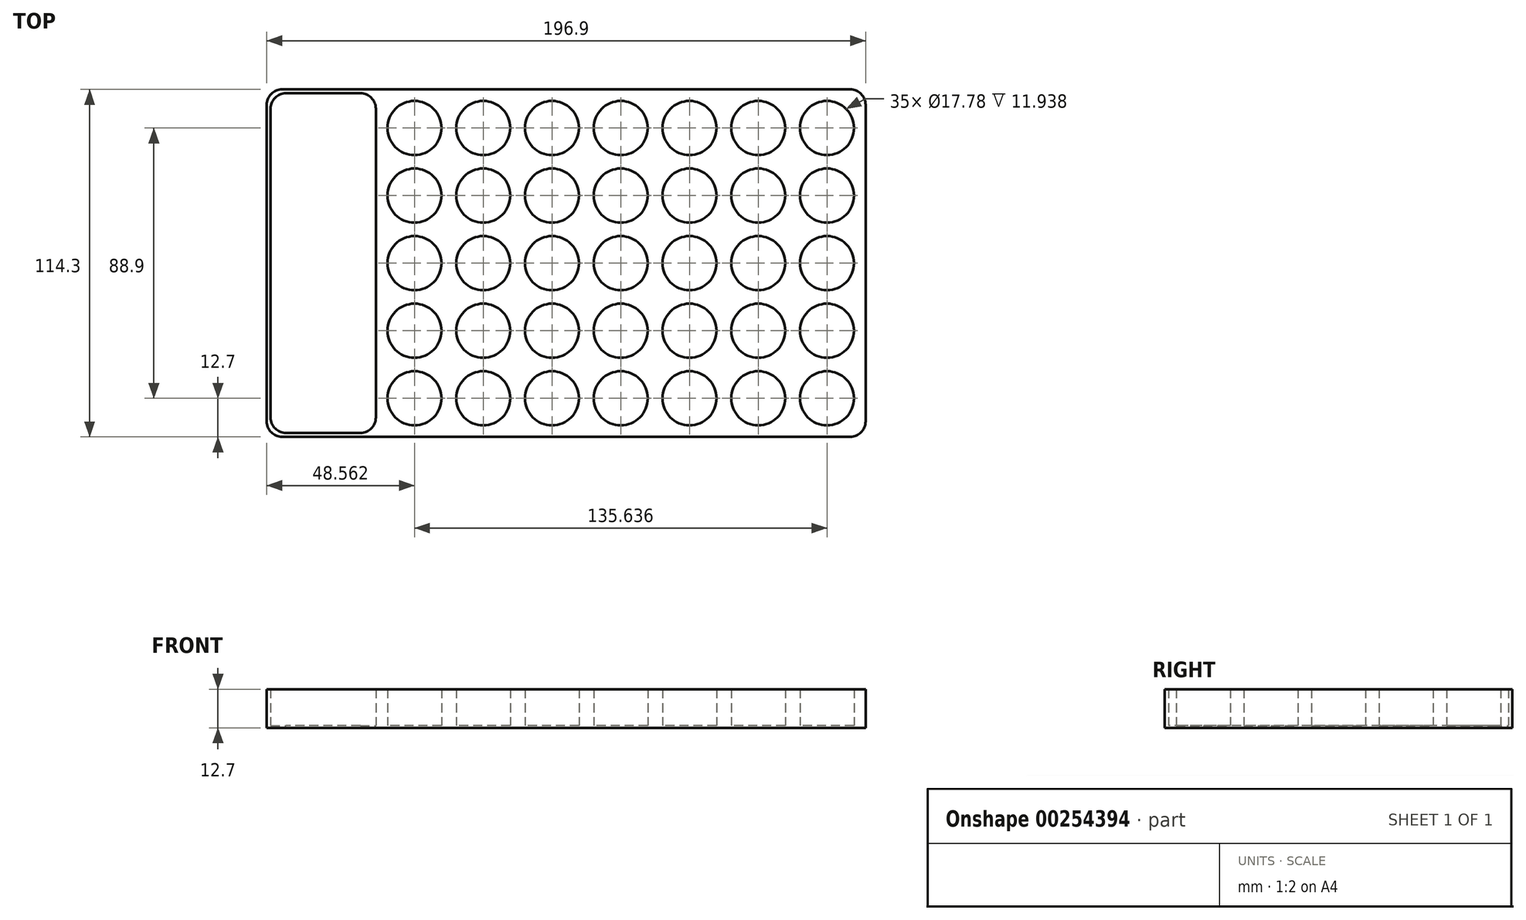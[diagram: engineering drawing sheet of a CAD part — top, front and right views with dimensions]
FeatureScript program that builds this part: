
annotation { "Feature Type Name" : "Feature", "Feature Type Description" : "" }
export const myFeature = defineFeature(function(context is Context, id is Id, definition is map)
    precondition{}
    {
        {
            var Q0;
            Q0=qCreatedBy(makeId("Top.planeOp"),FACE);
            var sketch = newSketch(context, id + "F0", { "sketchPlane" : qUnion([Q0])});
            skLineSegment(sketch, "E0.bottom", {"start": v(80.52, 57.15) * mm, "end": v(-80.52, 57.15) * mm});
            skLineSegment(sketch, "E0.top", {"start": v(80.52, -57.15) * mm, "end": v(-80.52, -57.15) * mm});
            skLineSegment(sketch, "E0.left", {"start": v(80.52, 57.15) * mm, "end": v(80.52, -57.15) * mm});
            skLineSegment(sketch, "E0.right", {"start": v(-80.52, 57.15) * mm, "end": v(-80.52, -57.15) * mm});
            skPoint(sketch, "E0.middle", {"position": v(0, 0) * mm});
            skCircle(sketch, "E1", {"center": v(-67.82, 44.45) * mm, "radius": 8.9 * mm});
            skCircle(sketch, "E2.0.1.0", {"center": v(-67.82, 22.22) * mm, "radius": 8.9 * mm});
            skCircle(sketch, "E2.0.2.0", {"center": v(-67.82, 0) * mm, "radius": 8.9 * mm});
            skCircle(sketch, "E2.0.3.0", {"center": v(-67.82, -22.23) * mm, "radius": 8.9 * mm});
            skCircle(sketch, "E2.0.4.0", {"center": v(-67.82, -44.45) * mm, "radius": 8.9 * mm});
            skCircle(sketch, "E2.1.0.0", {"center": v(-45.21, 44.45) * mm, "radius": 8.9 * mm});
            skCircle(sketch, "E2.1.1.0", {"center": v(-45.21, 22.22) * mm, "radius": 8.9 * mm});
            skCircle(sketch, "E2.1.2.0", {"center": v(-45.21, 0) * mm, "radius": 8.9 * mm});
            skCircle(sketch, "E2.1.3.0", {"center": v(-45.21, -22.23) * mm, "radius": 8.9 * mm});
            skCircle(sketch, "E2.1.4.0", {"center": v(-45.21, -44.45) * mm, "radius": 8.9 * mm});
            skCircle(sketch, "E2.2.0.0", {"center": v(-22.6, 44.45) * mm, "radius": 8.9 * mm});
            skCircle(sketch, "E2.2.1.0", {"center": v(-22.6, 22.22) * mm, "radius": 8.9 * mm});
            skCircle(sketch, "E2.2.2.0", {"center": v(-22.6, 0) * mm, "radius": 8.9 * mm});
            skCircle(sketch, "E2.2.3.0", {"center": v(-22.6, -22.23) * mm, "radius": 8.9 * mm});
            skCircle(sketch, "E2.2.4.0", {"center": v(-22.6, -44.45) * mm, "radius": 8.9 * mm});
            skCircle(sketch, "E2.3.0.0", {"center": v(0, 44.45) * mm, "radius": 8.9 * mm});
            skCircle(sketch, "E2.3.1.0", {"center": v(0, 22.22) * mm, "radius": 8.9 * mm});
            skCircle(sketch, "E2.3.2.0", {"center": v(0, 0) * mm, "radius": 8.9 * mm});
            skCircle(sketch, "E2.3.3.0", {"center": v(0, -22.23) * mm, "radius": 8.9 * mm});
            skCircle(sketch, "E2.3.4.0", {"center": v(0, -44.45) * mm, "radius": 8.9 * mm});
            skCircle(sketch, "E2.4.0.0", {"center": v(22.6, 44.45) * mm, "radius": 8.9 * mm});
            skCircle(sketch, "E2.4.1.0", {"center": v(22.6, 22.22) * mm, "radius": 8.9 * mm});
            skCircle(sketch, "E2.4.2.0", {"center": v(22.6, 0) * mm, "radius": 8.9 * mm});
            skCircle(sketch, "E2.4.3.0", {"center": v(22.6, -22.23) * mm, "radius": 8.9 * mm});
            skCircle(sketch, "E2.4.4.0", {"center": v(22.6, -44.45) * mm, "radius": 8.9 * mm});
            skCircle(sketch, "E2.5.0.0", {"center": v(45.21, 44.45) * mm, "radius": 8.9 * mm});
            skCircle(sketch, "E2.5.1.0", {"center": v(45.21, 22.22) * mm, "radius": 8.9 * mm});
            skCircle(sketch, "E2.5.2.0", {"center": v(45.21, 0) * mm, "radius": 8.9 * mm});
            skCircle(sketch, "E2.5.3.0", {"center": v(45.21, -22.23) * mm, "radius": 8.9 * mm});
            skCircle(sketch, "E2.5.4.0", {"center": v(45.21, -44.45) * mm, "radius": 8.9 * mm});
            skCircle(sketch, "E2.6.0.0", {"center": v(67.82, 44.45) * mm, "radius": 8.9 * mm});
            skCircle(sketch, "E2.6.1.0", {"center": v(67.82, 22.22) * mm, "radius": 8.9 * mm});
            skCircle(sketch, "E2.6.2.0", {"center": v(67.82, 0) * mm, "radius": 8.9 * mm});
            skCircle(sketch, "E2.6.3.0", {"center": v(67.82, -22.23) * mm, "radius": 8.9 * mm});
            skCircle(sketch, "E2.6.4.0", {"center": v(67.82, -44.45) * mm, "radius": 8.9 * mm});
            skLineSegment(sketch, "E2.direction1", {"start": v(-53.34, 40.64) * mm, "end": v(-30.73, 40.64) * mm, "construction": true});
            skLineSegment(sketch, "E2.direction2", {"start": v(-53.34, 40.64) * mm, "end": v(-53.34, 18.29) * mm, "construction": true});
            skLineSegment(sketch, "E3.bottom", {"start": v(-80.52, 57.15) * mm, "end": v(-116.38, 57.15) * mm});
            skLineSegment(sketch, "E3.top", {"start": v(-80.52, -57.15) * mm, "end": v(-116.38, -57.15) * mm});
            skLineSegment(sketch, "E3.right", {"start": v(-116.38, 57.15) * mm, "end": v(-116.38, -57.15) * mm});
            skLineSegment(sketch, "E4.bottom", {"start": v(-80.52, 55.88) * mm, "end": v(-115.1, 55.88) * mm});
            skLineSegment(sketch, "E4.top", {"start": v(-80.52, -55.88) * mm, "end": v(-115.1, -55.88) * mm});
            skLineSegment(sketch, "E4.left", {"start": v(-80.52, 55.88) * mm, "end": v(-80.52, -55.88) * mm});
            skLineSegment(sketch, "E4.right", {"start": v(-115.1, 55.88) * mm, "end": v(-115.1, -55.88) * mm});
            skSolve(sketch);
        }
        {
            var Q0;
            Q0=makeQuery(id+"F0.imprint","IMPRINT",FACE,{"disambiguationData":[TD([[makeQuery(id+"F0.imprint","IMPRINT",EDGE,{"derivedFrom":sQuery(id+"F0.wireOp",EDGE,"E0.bottom")}),1.0]])]});
            var Q1;
            {var subQ4=sQuery(id+"F0.wireOp",EDGE,"E3.bottom");Q1=makeQuery(id+"F0.imprint","IMPRINT",FACE,{"disambiguationData":[TD([[makeQuery(id+"F0.imprint","IMPRINT",EDGE,{"derivedFrom":subQ4}),1.0]])]});}
            extrude(context, id + "F1", {"entities" : qUnion([Q0, Q1]), "depth" : 12.7 * mm});
        }
        {
            var Q0;
            Q0=makeQuery(id+"F0.imprint","IMPRINT",FACE,{"disambiguationData":[TD([[makeQuery(id+"F0.imprint","IMPRINT",EDGE,{"derivedFrom":sQuery(id+"F0.wireOp",EDGE,"E1")}),1.0]])]});
            var Q1;
            Q1=makeQuery(id+"F0.imprint","IMPRINT",FACE,{"disambiguationData":[TD([[makeQuery(id+"F0.imprint","IMPRINT",EDGE,{"derivedFrom":sQuery(id+"F0.wireOp",EDGE,"E2.1.0.0")}),1.0]])]});
            var Q2;
            Q2=makeQuery(id+"F0.imprint","IMPRINT",FACE,{"disambiguationData":[TD([[makeQuery(id+"F0.imprint","IMPRINT",EDGE,{"derivedFrom":sQuery(id+"F0.wireOp",EDGE,"E2.2.0.0")}),1.0]])]});
            var Q3;
            Q3=makeQuery(id+"F0.imprint","IMPRINT",FACE,{"disambiguationData":[TD([[makeQuery(id+"F0.imprint","IMPRINT",EDGE,{"derivedFrom":sQuery(id+"F0.wireOp",EDGE,"E2.3.0.0")}),1.0]])]});
            var Q4;
            Q4=makeQuery(id+"F0.imprint","IMPRINT",FACE,{"disambiguationData":[TD([[makeQuery(id+"F0.imprint","IMPRINT",EDGE,{"derivedFrom":sQuery(id+"F0.wireOp",EDGE,"E2.4.0.0")}),1.0]])]});
            var Q5;
            Q5=makeQuery(id+"F0.imprint","IMPRINT",FACE,{"disambiguationData":[TD([[makeQuery(id+"F0.imprint","IMPRINT",EDGE,{"derivedFrom":sQuery(id+"F0.wireOp",EDGE,"E2.5.0.0")}),1.0]])]});
            var Q6;
            Q6=makeQuery(id+"F0.imprint","IMPRINT",FACE,{"disambiguationData":[TD([[makeQuery(id+"F0.imprint","IMPRINT",EDGE,{"derivedFrom":sQuery(id+"F0.wireOp",EDGE,"E2.6.0.0")}),1.0]])]});
            var Q7;
            Q7=makeQuery(id+"F0.imprint","IMPRINT",FACE,{"disambiguationData":[TD([[makeQuery(id+"F0.imprint","IMPRINT",EDGE,{"derivedFrom":sQuery(id+"F0.wireOp",EDGE,"E2.6.1.0")}),1.0]])]});
            var Q8;
            Q8=makeQuery(id+"F0.imprint","IMPRINT",FACE,{"disambiguationData":[TD([[makeQuery(id+"F0.imprint","IMPRINT",EDGE,{"derivedFrom":sQuery(id+"F0.wireOp",EDGE,"E2.5.1.0")}),1.0]])]});
            var Q9;
            Q9=makeQuery(id+"F0.imprint","IMPRINT",FACE,{"disambiguationData":[TD([[makeQuery(id+"F0.imprint","IMPRINT",EDGE,{"derivedFrom":sQuery(id+"F0.wireOp",EDGE,"E2.4.1.0")}),1.0]])]});
            var Q10;
            Q10=makeQuery(id+"F0.imprint","IMPRINT",FACE,{"disambiguationData":[TD([[makeQuery(id+"F0.imprint","IMPRINT",EDGE,{"derivedFrom":sQuery(id+"F0.wireOp",EDGE,"E2.3.1.0")}),1.0]])]});
            var Q11;
            Q11=makeQuery(id+"F0.imprint","IMPRINT",FACE,{"disambiguationData":[TD([[makeQuery(id+"F0.imprint","IMPRINT",EDGE,{"derivedFrom":sQuery(id+"F0.wireOp",EDGE,"E2.2.1.0")}),1.0]])]});
            var Q12;
            Q12=makeQuery(id+"F0.imprint","IMPRINT",FACE,{"disambiguationData":[TD([[makeQuery(id+"F0.imprint","IMPRINT",EDGE,{"derivedFrom":sQuery(id+"F0.wireOp",EDGE,"E2.1.1.0")}),1.0]])]});
            var Q13;
            Q13=makeQuery(id+"F0.imprint","IMPRINT",FACE,{"disambiguationData":[TD([[makeQuery(id+"F0.imprint","IMPRINT",EDGE,{"derivedFrom":sQuery(id+"F0.wireOp",EDGE,"E2.0.1.0")}),1.0]])]});
            var Q14;
            Q14=makeQuery(id+"F0.imprint","IMPRINT",FACE,{"disambiguationData":[TD([[makeQuery(id+"F0.imprint","IMPRINT",EDGE,{"derivedFrom":sQuery(id+"F0.wireOp",EDGE,"E2.0.2.0")}),1.0]])]});
            var Q15;
            Q15=makeQuery(id+"F0.imprint","IMPRINT",FACE,{"disambiguationData":[TD([[makeQuery(id+"F0.imprint","IMPRINT",EDGE,{"derivedFrom":sQuery(id+"F0.wireOp",EDGE,"E2.1.2.0")}),1.0]])]});
            var Q16;
            Q16=makeQuery(id+"F0.imprint","IMPRINT",FACE,{"disambiguationData":[TD([[makeQuery(id+"F0.imprint","IMPRINT",EDGE,{"derivedFrom":sQuery(id+"F0.wireOp",EDGE,"E2.2.2.0")}),1.0]])]});
            var Q17;
            Q17=makeQuery(id+"F0.imprint","IMPRINT",FACE,{"disambiguationData":[TD([[makeQuery(id+"F0.imprint","IMPRINT",EDGE,{"derivedFrom":sQuery(id+"F0.wireOp",EDGE,"E2.3.2.0")}),1.0]])]});
            var Q18;
            Q18=makeQuery(id+"F0.imprint","IMPRINT",FACE,{"disambiguationData":[TD([[makeQuery(id+"F0.imprint","IMPRINT",EDGE,{"derivedFrom":sQuery(id+"F0.wireOp",EDGE,"E2.4.2.0")}),1.0]])]});
            var Q19;
            Q19=makeQuery(id+"F0.imprint","IMPRINT",FACE,{"disambiguationData":[TD([[makeQuery(id+"F0.imprint","IMPRINT",EDGE,{"derivedFrom":sQuery(id+"F0.wireOp",EDGE,"E2.5.2.0")}),1.0]])]});
            var Q20;
            Q20=makeQuery(id+"F0.imprint","IMPRINT",FACE,{"disambiguationData":[TD([[makeQuery(id+"F0.imprint","IMPRINT",EDGE,{"derivedFrom":sQuery(id+"F0.wireOp",EDGE,"E2.6.2.0")}),1.0]])]});
            var Q21;
            Q21=makeQuery(id+"F0.imprint","IMPRINT",FACE,{"disambiguationData":[TD([[makeQuery(id+"F0.imprint","IMPRINT",EDGE,{"derivedFrom":sQuery(id+"F0.wireOp",EDGE,"E2.6.3.0")}),1.0]])]});
            var Q22;
            Q22=makeQuery(id+"F0.imprint","IMPRINT",FACE,{"disambiguationData":[TD([[makeQuery(id+"F0.imprint","IMPRINT",EDGE,{"derivedFrom":sQuery(id+"F0.wireOp",EDGE,"E2.5.3.0")}),1.0]])]});
            var Q23;
            Q23=makeQuery(id+"F0.imprint","IMPRINT",FACE,{"disambiguationData":[TD([[makeQuery(id+"F0.imprint","IMPRINT",EDGE,{"derivedFrom":sQuery(id+"F0.wireOp",EDGE,"E2.4.3.0")}),1.0]])]});
            var Q24;
            Q24=makeQuery(id+"F0.imprint","IMPRINT",FACE,{"disambiguationData":[TD([[makeQuery(id+"F0.imprint","IMPRINT",EDGE,{"derivedFrom":sQuery(id+"F0.wireOp",EDGE,"E2.3.3.0")}),1.0]])]});
            var Q25;
            Q25=makeQuery(id+"F0.imprint","IMPRINT",FACE,{"disambiguationData":[TD([[makeQuery(id+"F0.imprint","IMPRINT",EDGE,{"derivedFrom":sQuery(id+"F0.wireOp",EDGE,"E2.2.3.0")}),1.0]])]});
            var Q26;
            Q26=makeQuery(id+"F0.imprint","IMPRINT",FACE,{"disambiguationData":[TD([[makeQuery(id+"F0.imprint","IMPRINT",EDGE,{"derivedFrom":sQuery(id+"F0.wireOp",EDGE,"E2.1.3.0")}),1.0]])]});
            var Q27;
            Q27=makeQuery(id+"F0.imprint","IMPRINT",FACE,{"disambiguationData":[TD([[makeQuery(id+"F0.imprint","IMPRINT",EDGE,{"derivedFrom":sQuery(id+"F0.wireOp",EDGE,"E2.0.3.0")}),1.0]])]});
            var Q28;
            Q28=makeQuery(id+"F0.imprint","IMPRINT",FACE,{"disambiguationData":[TD([[makeQuery(id+"F0.imprint","IMPRINT",EDGE,{"derivedFrom":sQuery(id+"F0.wireOp",EDGE,"E2.0.4.0")}),1.0]])]});
            var Q29;
            Q29=makeQuery(id+"F0.imprint","IMPRINT",FACE,{"disambiguationData":[TD([[makeQuery(id+"F0.imprint","IMPRINT",EDGE,{"derivedFrom":sQuery(id+"F0.wireOp",EDGE,"E2.1.4.0")}),1.0]])]});
            var Q30;
            Q30=makeQuery(id+"F0.imprint","IMPRINT",FACE,{"disambiguationData":[TD([[makeQuery(id+"F0.imprint","IMPRINT",EDGE,{"derivedFrom":sQuery(id+"F0.wireOp",EDGE,"E2.2.4.0")}),1.0]])]});
            var Q31;
            Q31=makeQuery(id+"F0.imprint","IMPRINT",FACE,{"disambiguationData":[TD([[makeQuery(id+"F0.imprint","IMPRINT",EDGE,{"derivedFrom":sQuery(id+"F0.wireOp",EDGE,"E2.3.4.0")}),1.0]])]});
            var Q32;
            Q32=makeQuery(id+"F0.imprint","IMPRINT",FACE,{"disambiguationData":[TD([[makeQuery(id+"F0.imprint","IMPRINT",EDGE,{"derivedFrom":sQuery(id+"F0.wireOp",EDGE,"E2.4.4.0")}),1.0]])]});
            var Q33;
            Q33=makeQuery(id+"F0.imprint","IMPRINT",FACE,{"disambiguationData":[TD([[makeQuery(id+"F0.imprint","IMPRINT",EDGE,{"derivedFrom":sQuery(id+"F0.wireOp",EDGE,"E2.5.4.0")}),1.0]])]});
            var Q34;
            Q34=makeQuery(id+"F0.imprint","IMPRINT",FACE,{"disambiguationData":[TD([[makeQuery(id+"F0.imprint","IMPRINT",EDGE,{"derivedFrom":sQuery(id+"F0.wireOp",EDGE,"E2.6.4.0")}),1.0]])]});
            var Q35;
            Q35=makeQuery(id+"F0.imprint","IMPRINT",FACE,{"disambiguationData":[TD([[makeQuery(id+"F0.imprint","IMPRINT",EDGE,{"derivedFrom":sQuery(id+"F0.wireOp",EDGE,"E4.bottom")}),1.0]])]});
            extrude(context, id + "F2", {"entities" : qUnion([Q0, Q1, Q2, Q3, Q4, Q5, Q6, Q7, Q8, Q9, Q10, Q11, Q12, Q13, Q14, Q15, Q16, Q17, Q18, Q19, Q20, Q21, Q22, Q23, Q24, Q25, Q26, Q27, Q28, Q29, Q30, Q31, Q32, Q33, Q34, Q35]), "operationType" : NewBodyOperationType.ADD, "depth" : 0.76 * mm});
        }
        {
            var Q0;
            Q0=makeQuery(id+"F1.opExtrude","SWEPT_EDGE",EDGE,{"disambiguationData":[OSD([sQuery(id+"F0.wireOp",EDGE,"E0.bottom"),sQuery(id+"F0.wireOp",EDGE,"E0.left")])]});
            var Q1;
            Q1=makeQuery(id+"F1.opExtrude","SWEPT_EDGE",EDGE,{"disambiguationData":[OSD([sQuery(id+"F0.wireOp",EDGE,"E0.top"),sQuery(id+"F0.wireOp",EDGE,"E0.left")])]});
            var Q2;
            Q2=makeQuery(id+"F1.opExtrude","SWEPT_EDGE",EDGE,{"disambiguationData":[OSD([sQuery(id+"F0.wireOp",EDGE,"E0.right"),sQuery(id+"F0.wireOp",EDGE,"E4.top"),sQuery(id+"F0.wireOp",EDGE,"E4.left")])]});
            var Q3;
            Q3=makeQuery(id+"F1.opExtrude","SWEPT_EDGE",EDGE,{"disambiguationData":[OSD([sQuery(id+"F0.wireOp",EDGE,"E0.right"),sQuery(id+"F0.wireOp",EDGE,"E4.bottom"),sQuery(id+"F0.wireOp",EDGE,"E4.left")])]});
            var Q4;
            Q4=makeQuery(id+"F1.opExtrude","SWEPT_EDGE",EDGE,{"disambiguationData":[OSD([sQuery(id+"F0.wireOp",EDGE,"E4.bottom"),sQuery(id+"F0.wireOp",EDGE,"E4.right")])]});
            var Q5;
            Q5=makeQuery(id+"F1.opExtrude","SWEPT_EDGE",EDGE,{"disambiguationData":[OSD([sQuery(id+"F0.wireOp",EDGE,"E4.top"),sQuery(id+"F0.wireOp",EDGE,"E4.right")])]});
            var Q6;
            Q6=makeQuery(id+"F1.opExtrude","SWEPT_EDGE",EDGE,{"disambiguationData":[OSD([sQuery(id+"F0.wireOp",EDGE,"E3.top"),sQuery(id+"F0.wireOp",EDGE,"E3.right")])]});
            var Q7;
            Q7=makeQuery(id+"F1.opExtrude","SWEPT_EDGE",EDGE,{"disambiguationData":[OSD([sQuery(id+"F0.wireOp",EDGE,"E3.bottom"),sQuery(id+"F0.wireOp",EDGE,"E3.right")])]});
            fillet(context, id + "F3", {"entities" : qUnion([Q0, Q1, Q2, Q3, Q4, Q5, Q6, Q7]), "radius" : 5.08 * mm, "tangentPropagation" : true, "allowEdgeOverflow" : false});
        }
    });
